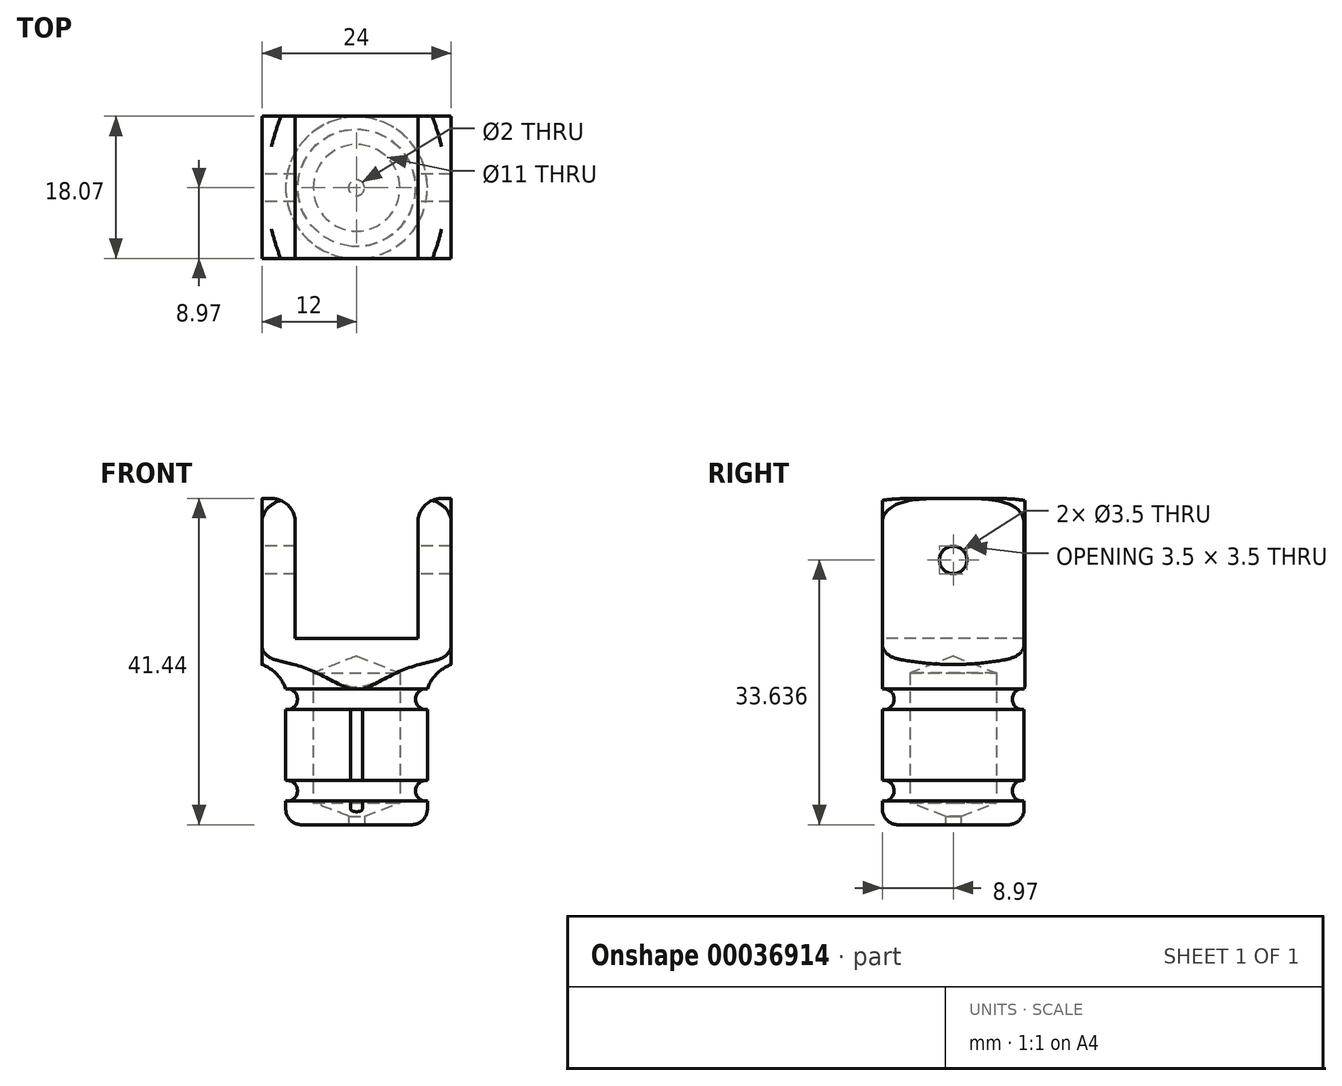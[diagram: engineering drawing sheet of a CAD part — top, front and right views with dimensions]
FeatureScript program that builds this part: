
annotation { "Feature Type Name" : "Feature", "Feature Type Description" : "" }
export const myFeature = defineFeature(function(context is Context, id is Id, definition is map)
    precondition{}
    {
        {
            var Q0;
            Q0=qCreatedBy(makeId("Front.planeOp"),FACE);
            var sketch = newSketch(context, id + "F0", { "sketchPlane" : qUnion([Q0])});
            skLineSegment(sketch, "E0", {"start": v(-15, 20) * mm, "end": v(-15, 0) * mm});
            skLineSegment(sketch, "E1", {"start": v(-15, 0) * mm, "end": v(-9, -2.18) * mm});
            skLineSegment(sketch, "E2", {"start": v(-9, -2.18) * mm, "end": v(-9, -4.18) * mm});
            skLineSegment(sketch, "E3", {"start": v(-9, -6.81) * mm, "end": v(-9, -15.81) * mm});
            skLineSegment(sketch, "E4", {"start": v(-9, -18.44) * mm, "end": v(-9, -21.44) * mm});
            skLineSegment(sketch, "E5", {"start": v(-9, -21.44) * mm, "end": v(-1, -21.44) * mm});
            skLineSegment(sketch, "E6", {"start": v(-1, -21.44) * mm, "end": v(-1, -20.35) * mm});
            skLineSegment(sketch, "E7", {"start": v(-1, -20.35) * mm, "end": v(-5.5, -18.64) * mm});
            skLineSegment(sketch, "E8", {"start": v(-5.5, -18.64) * mm, "end": v(-5.5, -2.18) * mm});
            skLineSegment(sketch, "E9", {"start": v(-5.5, -2.18) * mm, "end": v(0, 0) * mm});
            skLineSegment(sketch, "E10", {"start": v(0, 0) * mm, "end": v(0, 20) * mm});
            skLineSegment(sketch, "E11", {"start": v(0, 20) * mm, "end": v(-15, 20) * mm});
            skLineSegment(sketch, "E12", {"start": v(-15, 20) * mm, "end": v(-15, 20) * mm});
            skArc(sketch, "E13", {"start": v(-9, -18.44) * mm, "mid": v(-7.5, -17.12) * mm, "end": v(-9, -15.81) * mm});
            skArc(sketch, "E14", {"start": v(-9, -6.81) * mm, "mid": v(-7.5, -5.5) * mm, "end": v(-9, -4.18) * mm});
            skLineSegment(sketch, "E15", {"start": v(-15, 0) * mm, "end": v(0, 0) * mm, "construction": true});
            skLineSegment(sketch, "E16", {"start": v(-9, -2.18) * mm, "end": v(-5.5, -2.18) * mm, "construction": true});
            skLineSegment(sketch, "E17", {"start": v(-7.5, -3.98) * mm, "end": v(-7.5, -18.64) * mm, "construction": true});
            skLineSegment(sketch, "E18", {"start": v(-9, -2.18) * mm, "end": v(-9, -21.44) * mm, "construction": true});
            skLineSegment(sketch, "E19", {"start": v(-7.5, -18.64) * mm, "end": v(-5.5, -18.64) * mm, "construction": true});
            skSolve(sketch);
        }
        {
            var Q0;
            Q0=makeQuery(id+"F0.imprint","IMPRINT",FACE,{"disambiguationData":[TD([[makeQuery(id+"F0.imprint","IMPRINT",EDGE,{"derivedFrom":sQuery(id+"F0.wireOp",EDGE,"E0")}),1.0]])]});
            var Q1;
            Q1=sQuery(id+"F0.wireOp",EDGE,"E10");
            revolve(context, id + "F1", {"entities" : qUnion([Q0]), "axis" : qUnion([Q1]), "revolveType" : RevolveType.FULL});
        }
        {
            var Q0;
            Q0=qCreatedBy(makeId("Front.planeOp"),FACE);
            var sketch = newSketch(context, id + "F2", { "sketchPlane" : qUnion([Q0])});
            skLineSegment(sketch, "E20.bottom", {"start": v(-7.8, 20.2) * mm, "end": v(7.8, 20.2) * mm});
            skLineSegment(sketch, "E20.top", {"start": v(-7.8, 2.2) * mm, "end": v(7.8, 2.2) * mm});
            skLineSegment(sketch, "E20.left", {"start": v(-7.8, 20.2) * mm, "end": v(-7.8, 2.2) * mm});
            skLineSegment(sketch, "E20.right", {"start": v(7.8, 20.2) * mm, "end": v(7.8, 2.2) * mm});
            skSolve(sketch);
        }
        {
            var Q0;
            Q0=qSketchRegion(id+"F2",true);
            extrude(context, id + "F3", {"entities" : qUnion([Q0]), "operationType" : NewBodyOperationType.REMOVE, "endBound" : BoundingType.SYMMETRIC, "oppositeDirection" : true, "depth" : 40 * mm});
        }
        {
            var Q0;
            Q0=makeQuery(id+"F3.boolean.opBoolean","COPY",FACE,{"derivedFrom":makeQuery(id+"F3.opExtrude","SWEPT_FACE",FACE,{"disambiguationData":[OSD([sQuery(id+"F2.wireOp",EDGE,"E20.right")])]})});
            var sketch = newSketch(context, id + "F4", { "sketchPlane" : qUnion([Q0])});
            skCircle(sketch, "E21", {"center": v(0, 12.2) * mm, "radius": 1.75 * mm});
            skSolve(sketch);
        }
        {
            var Q0;
            Q0=qSketchRegion(id+"F4",true);
            extrude(context, id + "F5", {"entities" : qUnion([Q0]), "operationType" : NewBodyOperationType.REMOVE, "endBound" : BoundingType.SYMMETRIC, "oppositeDirection" : true, "depth" : 50 * mm});
        }
        {
            var Q0;
            Q0=makeQuery(id+"F1.opRevolve","SWEPT_EDGE",EDGE,{"disambiguationData":[OSD([sQuery(id+"F0.wireOp",EDGE,"E4"),sQuery(id+"F0.wireOp",EDGE,"E5")])]});
            var Q1;
            Q1=makeQuery(id+"F1.opRevolve","SWEPT_EDGE",EDGE,{"disambiguationData":[OSD([sQuery(id+"F0.wireOp",EDGE,"E0"),sQuery(id+"F0.wireOp",EDGE,"E1")])]});
            fillet(context, id + "F6", {"entities" : qUnion([Q0, Q1]), "radius" : 2 * mm, "tangentPropagation" : true, "allowEdgeOverflow" : false});
        }
        {
            var Q0;
            Q0=makeQuery(id+"F1.opRevolve","SWEPT_EDGE",EDGE,{"disambiguationData":[OSD([sQuery(id+"F0.wireOp",EDGE,"E1"),sQuery(id+"F0.wireOp",EDGE,"E2")])]});
            fillet(context, id + "F7", {"entities" : qUnion([Q0]), "radius" : 5 * mm, "tangentPropagation" : true, "allowEdgeOverflow" : false});
        }
        {
            var Q0;
            Q0=makeQuery(id+"F3.boolean.opBoolean","INTERSECT",EDGE,{"disambiguationData":[OD(0.0)],"derivedFrom":[makeQuery(id+"F1.opRevolve","SWEPT_FACE",FACE,{"disambiguationData":[OSD([sQuery(id+"F0.wireOp",EDGE,"E0")])]}),makeQuery(id+"F3.opExtrude","SWEPT_FACE",FACE,{"disambiguationData":[OSD([sQuery(id+"F2.wireOp",EDGE,"E20.top")])]})]});
            var Q1;
            Q1=makeQuery(id+"F3.boolean.opBoolean","INTERSECT",EDGE,{"disambiguationData":[OD(1.0)],"derivedFrom":[makeQuery(id+"F1.opRevolve","SWEPT_FACE",FACE,{"disambiguationData":[OSD([sQuery(id+"F0.wireOp",EDGE,"E0")])]}),makeQuery(id+"F3.opExtrude","SWEPT_FACE",FACE,{"disambiguationData":[OSD([sQuery(id+"F2.wireOp",EDGE,"E20.top")])]})]});
            fillet(context, id + "F8", {"entities" : qUnion([Q0, Q1]), "radius" : 1 * mm, "tangentPropagation" : true, "allowEdgeOverflow" : false});
        }
        {
            var Q0;
            Q0=makeQuery(id+"F3.boolean.opBoolean","INTERSECT",EDGE,{"derivedFrom":[makeQuery(id+"F1.opRevolve","SWEPT_FACE",FACE,{"disambiguationData":[OSD([sQuery(id+"F0.wireOp",EDGE,"E11")])]}),makeQuery(id+"F3.opExtrude","SWEPT_FACE",FACE,{"disambiguationData":[OSD([sQuery(id+"F2.wireOp",EDGE,"E20.left")])]})]});
            var Q1;
            {var subQ0=sQuery(id+"F0.wireOp",EDGE,"E0");var subQ1=sQuery(id+"F0.wireOp",EDGE,"E11");Q1=makeQuery(id+"F3.boolean.opBoolean","SPLIT",EDGE,{"disambiguationData":[TD([makeQuery(id+"F3.opExtrude","SWEPT_FACE",FACE,{"disambiguationData":[OSD([sQuery(id+"F2.wireOp",EDGE,"E20.left")])]})])],"derivedFrom":makeQuery(id+"F1.opRevolve","SWEPT_EDGE",EDGE,{"disambiguationData":[OSD([subQ0,subQ1])]})});}
            var Q2;
            Q2=makeQuery(id+"F3.boolean.opBoolean","INTERSECT",EDGE,{"derivedFrom":[makeQuery(id+"F1.opRevolve","SWEPT_FACE",FACE,{"disambiguationData":[OSD([sQuery(id+"F0.wireOp",EDGE,"E11")])]}),makeQuery(id+"F3.opExtrude","SWEPT_FACE",FACE,{"disambiguationData":[OSD([sQuery(id+"F2.wireOp",EDGE,"E20.right")])]})]});
            var Q3;
            {var subQ0=sQuery(id+"F0.wireOp",EDGE,"E0");var subQ1=sQuery(id+"F0.wireOp",EDGE,"E11");Q3=makeQuery(id+"F3.boolean.opBoolean","SPLIT",EDGE,{"disambiguationData":[TD([makeQuery(id+"F3.opExtrude","SWEPT_FACE",FACE,{"disambiguationData":[OSD([sQuery(id+"F2.wireOp",EDGE,"E20.right")])]})])],"derivedFrom":makeQuery(id+"F1.opRevolve","SWEPT_EDGE",EDGE,{"disambiguationData":[OSD([subQ0,subQ1])]})});}
            fillet(context, id + "F9", {"entities" : qUnion([Q0, Q1, Q2, Q3]), "radius" : 3 * mm, "tangentPropagation" : true, "allowEdgeOverflow" : false});
        }
        {
            var Q0;
            Q0=qCreatedBy(makeId("Right.planeOp"),FACE);
            var sketch = newSketch(context, id + "F10", { "sketchPlane" : qUnion([Q0])});
            skLineSegment(sketch, "E22.bottom", {"start": v(-8.97, 22.85) * mm, "end": v(9.1, 22.85) * mm});
            skLineSegment(sketch, "E22.top", {"start": v(-8.97, -22.36) * mm, "end": v(9.1, -22.36) * mm});
            skLineSegment(sketch, "E22.left", {"start": v(-8.97, 22.85) * mm, "end": v(-8.97, -22.36) * mm});
            skLineSegment(sketch, "E22.right", {"start": v(9.1, 22.85) * mm, "end": v(9.1, -22.36) * mm});
            skSolve(sketch);
        }
        {
            var Q0;
            Q0=qSketchRegion(id+"F10",true);
            extrude(context, id + "F11", {"entities" : qUnion([Q0]), "operationType" : NewBodyOperationType.INTERSECT, "endBound" : BoundingType.SYMMETRIC, "oppositeDirection" : true, "depth" : 24 * mm});
        }
    });
